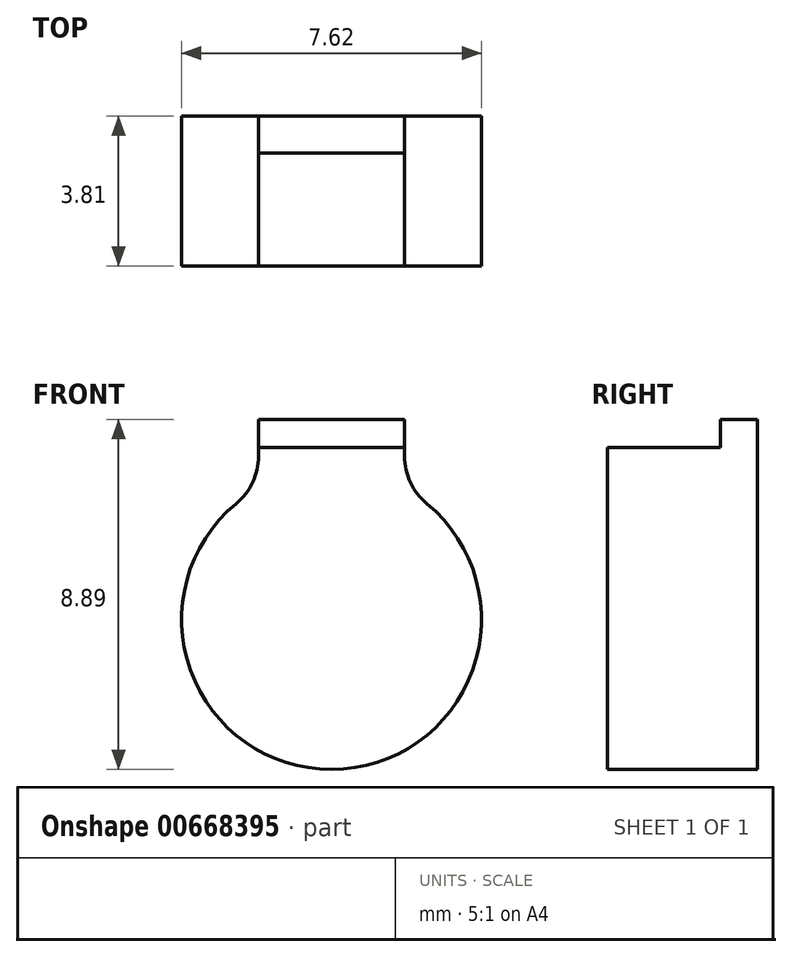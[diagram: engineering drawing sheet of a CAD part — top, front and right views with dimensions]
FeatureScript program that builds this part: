
annotation { "Feature Type Name" : "Feature", "Feature Type Description" : "" }
export const myFeature = defineFeature(function(context is Context, id is Id, definition is map)
    precondition{}
    {
        {
            var Q0;
            Q0=qCreatedBy(makeId("Front.planeOp"),FACE);
            var sketch = newSketch(context, id + "F0", { "sketchPlane" : qUnion([Q0])});
            skCircle(sketch, "E0", {"center": v(0, 0) * mm, "radius": 3.81 * mm});
            skLineSegment(sketch, "E1", {"start": v(0, 3.81) * mm, "end": v(0, 5.08) * mm});
            skLineSegment(sketch, "E2", {"start": v(0, 5.08) * mm, "end": v(-1.85, 5.08) * mm});
            skLineSegment(sketch, "E3", {"start": v(-1.85, 5.08) * mm, "end": v(-1.85, 3.33) * mm});
            skLineSegment(sketch, "E4.MirrorCS", {"start": v(0, 5.08) * mm, "end": v(1.85, 5.08) * mm});
            skLineSegment(sketch, "E5.MirrorCS", {"start": v(1.85, 5.08) * mm, "end": v(1.85, 3.33) * mm});
            skSolve(sketch);
        }
        {
            var Q0;
            Q0 = qSketchRegion(id + "F0", true);
            extrude(context, id + "F1", {"entities" : qUnion([Q0]), "depth" : -3.8 * mm, "offsetDistance" : 25.4 * mm});
        }
        {
            var Q0;
            Q0=makeQuery(id+"F1.opExtrude","SWEPT_EDGE",EDGE,{"disambiguationData":[OSD([sQuery(id+"F0.wireOp",EDGE,"E0"),sQuery(id+"F0.wireOp",EDGE,"E5.MirrorCS")])]});
            var Q1;
            Q1=makeQuery(id+"F1.opExtrude","SWEPT_EDGE",EDGE,{"disambiguationData":[OSD([sQuery(id+"F0.wireOp",EDGE,"E0"),sQuery(id+"F0.wireOp",EDGE,"E3")])]});
            fillet(context, id + "F2", {"entities" : qUnion([Q0, Q1]), "radius" : 1.57 * mm, "tangentPropagation" : true, "allowEdgeOverflow" : false});
        }
        {
            var Q0;
            Q0=makeQuery(id+"F1.opExtrude","SWEPT_FACE",FACE,{"disambiguationData":[OSD([sQuery(id+"F0.wireOp",EDGE,"E2"),sQuery(id+"F0.wireOp",EDGE,"E4.MirrorCS")])]});
            var sketch = newSketch(context, id + "F3", { "sketchPlane" : qUnion([Q0])});
            skLineSegment(sketch, "E6", {"start": v(-1.85, 2.87) * mm, "end": v(1.85, 2.87) * mm});
            skLineSegment(sketch, "E7", {"start": v(-1.85, 2.87) * mm, "end": v(-1.85, 3.81) * mm});
            skLineSegment(sketch, "E8", {"start": v(-1.85, 3.81) * mm, "end": v(1.85, 3.81) * mm});
            skLineSegment(sketch, "E9", {"start": v(1.85, 3.81) * mm, "end": v(1.85, 2.87) * mm});
            skSolve(sketch);
        }
        {
            var Q0;
            {var subQ0=sQuery(id+"F3.wireOp",EDGE,"E6");Q0=makeQuery(id+"F3.imprint","IMPRINT",FACE,{"disambiguationData":[TD([[makeQuery(id+"F3.imprint","IMPRINT",EDGE,{"derivedFrom":subQ0}),-1.0]])]});}
            var sketch = newSketch(context, id + "F4", { "sketchPlane" : qUnion([Q0])});
            skSolve(sketch);
        }
        {
            var Q0;
            Q0 = qSketchRegion(id + "F4", true);
            var Q1;
            {var subQ0=sQuery(id+"F3.wireOp",EDGE,"E6");Q1=makeQuery(id+"F4.imprint","IMPRINT",FACE,{"disambiguationData":[TD([[makeQuery(id+"F4.imprint","IMPRINT",EDGE,{"derivedFrom":makeQuery(id+"F3.imprint","IMPRINT",EDGE,{"derivedFrom":subQ0})}),-1.0]])]});}
            extrude(context, id + "F5", {"entities" : qUnion([Q0, Q1]), "operationType" : NewBodyOperationType.REMOVE, "oppositeDirection" : true, "depth" : 0.71 * mm, "offsetDistance" : 25.4 * mm});
        }
    });
